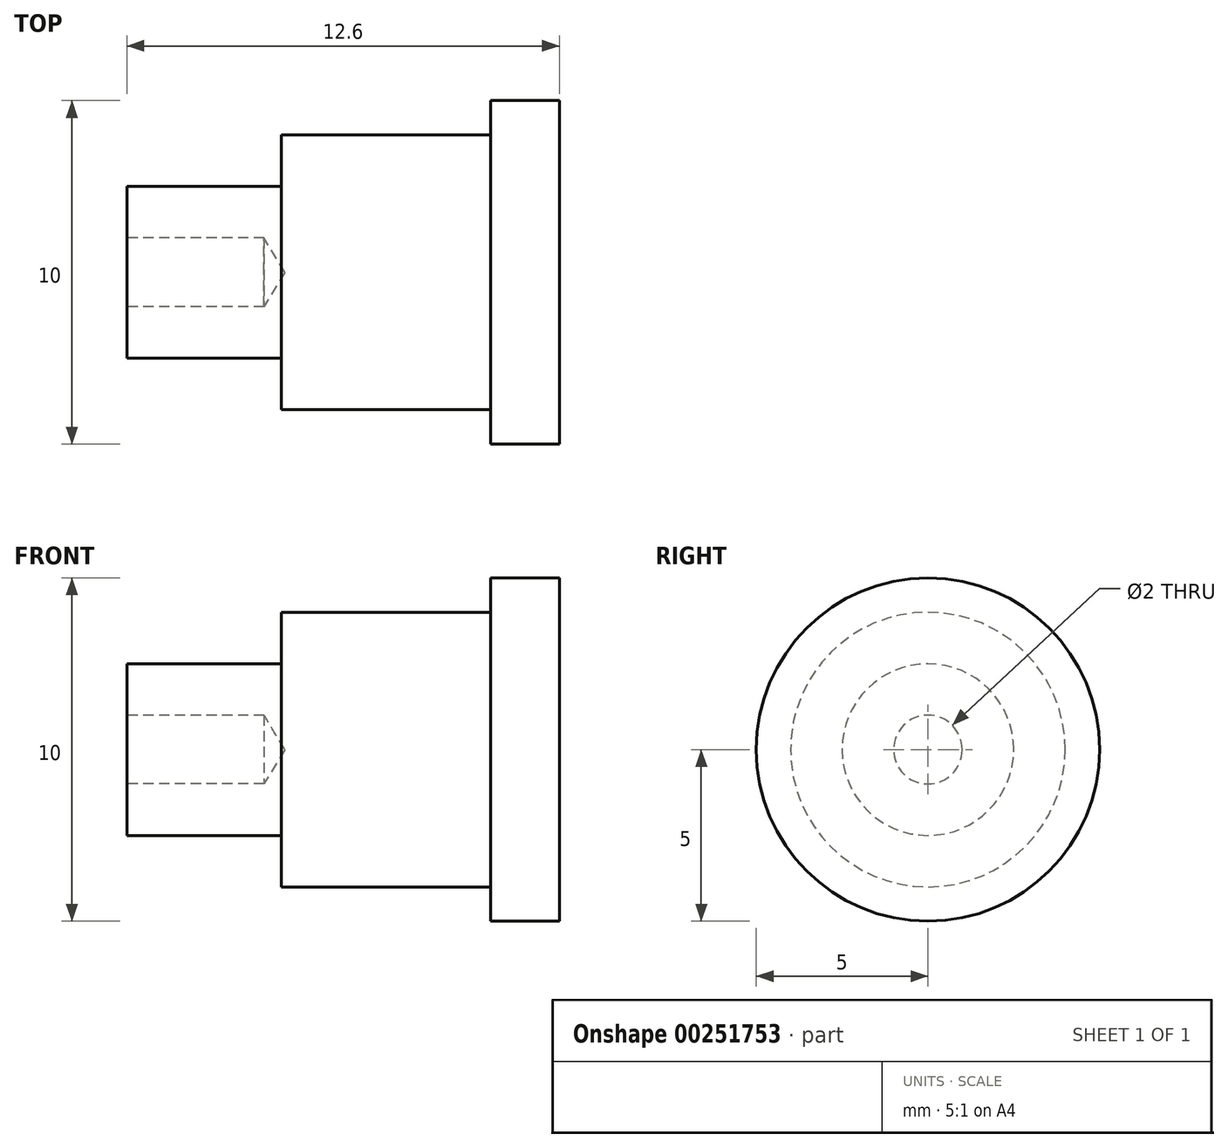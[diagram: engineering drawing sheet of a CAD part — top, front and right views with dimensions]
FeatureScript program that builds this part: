
annotation { "Feature Type Name" : "Feature", "Feature Type Description" : "" }
export const myFeature = defineFeature(function(context is Context, id is Id, definition is map)
    precondition{}
    {
        {
            var Q0;
            Q0=qCreatedBy(makeId("Front.planeOp"),FACE);
            var sketch = newSketch(context, id + "F0", { "sketchPlane" : qUnion([Q0])});
            skLineSegment(sketch, "E0", {"start": v(-7.5, 0) * mm, "end": v(-7.5, 2.5) * mm});
            skLineSegment(sketch, "E1", {"start": v(-7.5, 2.5) * mm, "end": v(-3, 2.5) * mm});
            skLineSegment(sketch, "E2", {"start": v(-3, 2.5) * mm, "end": v(-3, 4) * mm});
            skLineSegment(sketch, "E3", {"start": v(-3, 4) * mm, "end": v(3.1, 4) * mm});
            skLineSegment(sketch, "E4", {"start": v(3.1, 4) * mm, "end": v(3.1, 5) * mm});
            skLineSegment(sketch, "E5", {"start": v(3.1, 5) * mm, "end": v(5.1, 5) * mm});
            skLineSegment(sketch, "E6", {"start": v(5.1, 5) * mm, "end": v(5.1, 0) * mm});
            skLineSegment(sketch, "E7", {"start": v(5.1, 0) * mm, "end": v(-7.5, 0) * mm});
            skSolve(sketch);
        }
        {
            var Q0;
            Q0=makeQuery(id+"F0.imprint","IMPRINT",FACE,{"disambiguationData":[TD([[makeQuery(id+"F0.imprint","IMPRINT",EDGE,{"derivedFrom":sQuery(id+"F0.wireOp",EDGE,"E0")}),-1.0]])]});
            var Q1;
            Q1=sQuery(id+"F0.wireOp",EDGE,"E7");
            revolve(context, id + "F1", {"entities" : qUnion([Q0]), "axis" : qUnion([Q1]), "revolveType" : RevolveType.FULL});
        }
        {
            var Q0;
            Q0=makeQuery(id+"F1.opRevolve","SWEPT_FACE",FACE,{"disambiguationData":[OSD([sQuery(id+"F0.wireOp",EDGE,"E0")])]});
            var sketch = newSketch(context, id + "F2", { "sketchPlane" : qUnion([Q0])});
            skPoint(sketch, "E8", {"position": v(0, 0) * mm});
            skSolve(sketch);
        }
        {
            var Q0;
            Q0=sQuery(id+"F2.wireOp",VERTEX,"E8");
            var Q1;
            Q1=makeQuery(id+"F1.opRevolve","SWEPT_BODY",BODY,{"disambiguationData":[OSD([sQuery(id+"F0.wireOp",EDGE,"E0"),sQuery(id+"F0.wireOp",EDGE,"E1"),sQuery(id+"F0.wireOp",EDGE,"E2"),sQuery(id+"F0.wireOp",EDGE,"E3"),sQuery(id+"F0.wireOp",EDGE,"E4"),sQuery(id+"F0.wireOp",EDGE,"E5"),sQuery(id+"F0.wireOp",EDGE,"E6"),sQuery(id+"F0.wireOp",EDGE,"E7")])]});
            hole(context, id + "F3", {"style" : HoleStyle.SIMPLE, "endStyle" : HoleEndStyle.BLIND, "holeDiameter" : 2 * mm, "holeDepth" : 4 * mm, "isTappedThrough" : true, "tappedDepth" : 12 * mm, "tapClearance" : 3, "locations" : qUnion([Q0]), "scope" : qUnion([Q1])});
        }
    });
